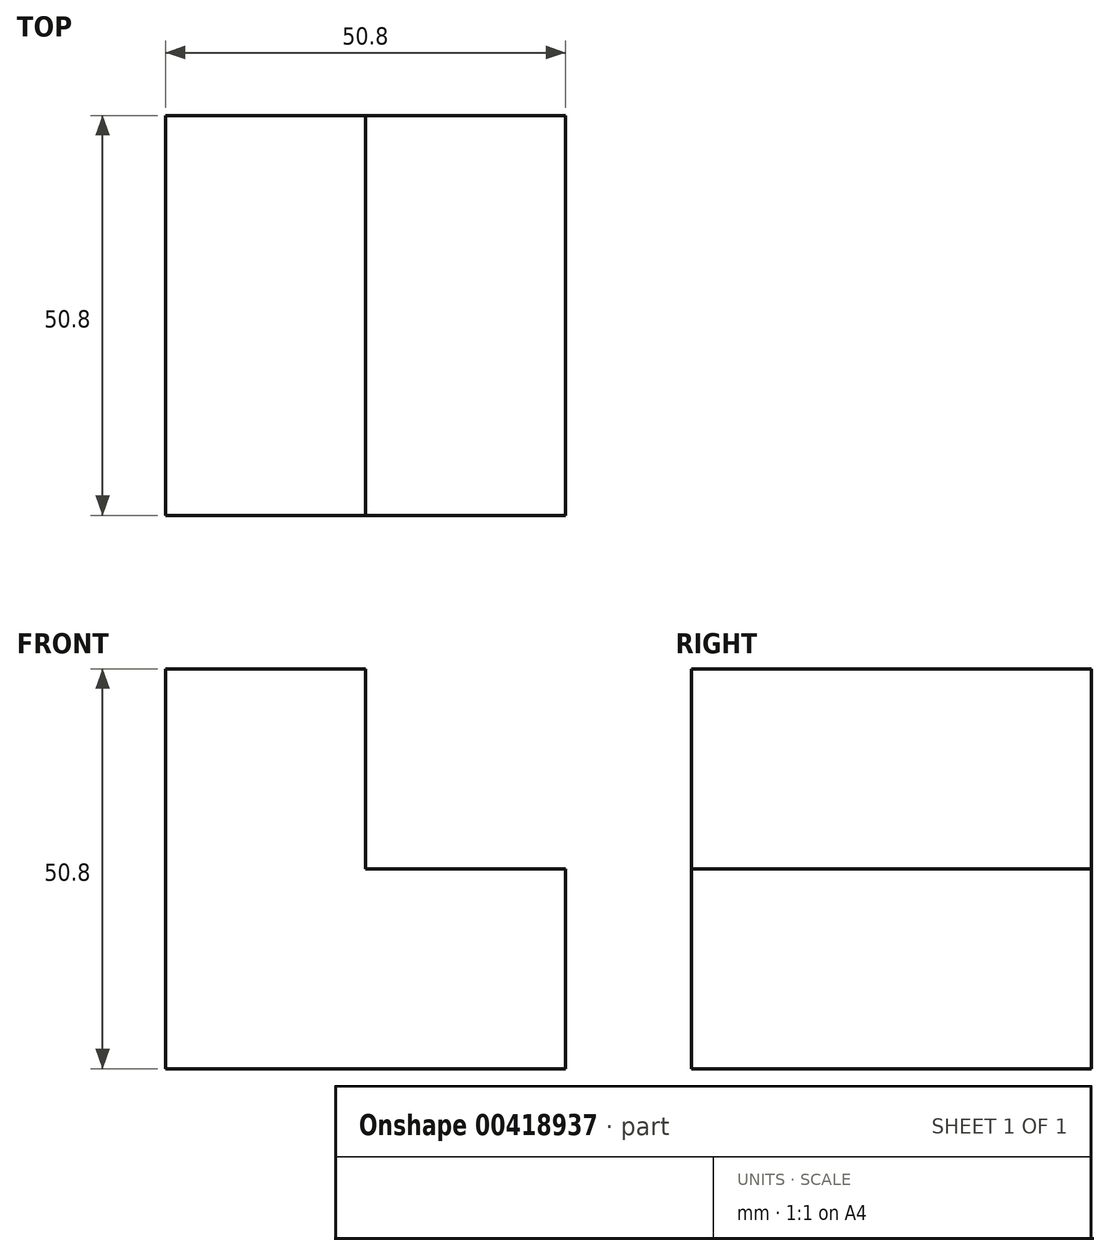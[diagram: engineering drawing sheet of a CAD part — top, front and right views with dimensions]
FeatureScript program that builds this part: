
annotation { "Feature Type Name" : "Feature", "Feature Type Description" : "" }
export const myFeature = defineFeature(function(context is Context, id is Id, definition is map)
    precondition{}
    {
        {
            var Q0;
            Q0=qCreatedBy(makeId("Front.planeOp"),FACE);
            var sketch = newSketch(context, id + "F0", { "sketchPlane" : qUnion([Q0])});
            skLineSegment(sketch, "E0", {"start": v(-75.8, 50.8) * mm, "end": v(-75.8, 0) * mm});
            skLineSegment(sketch, "E1", {"start": v(-75.8, 0) * mm, "end": v(-25, 0) * mm});
            skLineSegment(sketch, "E2", {"start": v(-75.8, 50.8) * mm, "end": v(-50.4, 50.8) * mm});
            skLineSegment(sketch, "E3", {"start": v(-50.4, 50.8) * mm, "end": v(-50.4, 25.4) * mm});
            skLineSegment(sketch, "E4", {"start": v(-50.4, 25.4) * mm, "end": v(-25, 25.4) * mm});
            skLineSegment(sketch, "E5", {"start": v(-25, 25.4) * mm, "end": v(-25, 0) * mm});
            skSolve(sketch);
        }
        {
            var Q0;
            Q0=makeQuery(id+"F0.imprint","IMPRINT",FACE,{"disambiguationData":[TD([[makeQuery(id+"F0.imprint","IMPRINT",EDGE,{"derivedFrom":sQuery(id+"F0.wireOp",EDGE,"E0")}),1.0]])]});
            extrude(context, id + "F1", {"entities" : qUnion([Q0]), "depth" : 50.8 * mm});
        }
    });
